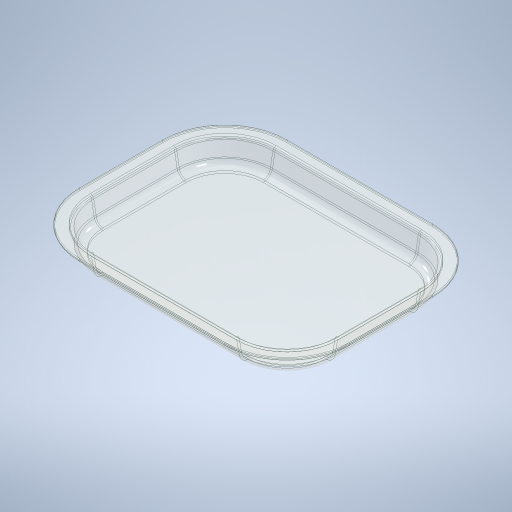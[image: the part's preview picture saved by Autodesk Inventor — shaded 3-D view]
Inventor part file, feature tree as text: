
AUTODESK INVENTOR PART (.ipt)
format: ipt  version: 2024 (Build 280153000, 153)  size: 461,312 bytes
history: native  units: mm
features: other x7, fillet x5, plane x3, sketch x3, mirror x2, extrude x1, shell x1, sweep x1, pattern_circular x1, revolve x1, loft x1, projected_geometry x1
ambient origin geometry x8: Origin, YZ Plane, XZ Plane, XY Plane, X Axis, Y Axis, Z Axis, Center Point
bodies: Volumenkörper1 (feature_tree)
feature tree (27):
  extrude  "Extrusion1"  Depth=70.0mm
  fillet  "Rundung1"  Radius=33.5mm
  other  "Flächenverjüngung1"
  fillet  "Rundung2"  Radius=70.0mm
  shell  "Wandung1"  Thickness=-1.745329mm
  sweep  "Sweeping1"
  fillet  "Rundung3"  Radius=20.0mm
  fillet  "Rundung4"  Radius=3.5mm
  fillet  "Rundung5"  [1 undecoded]
  plane  "Arbeitsebene1"
  plane  "Arbeitsebene2"
  plane  "Arbeitsebene3"
  other  "Trennen1"
  other  "Trennen2"
  other  "Trennen3"
  pattern_circular  "Runde Anordnung1"  [2 undecoded]
  revolve  "Umdrehung1"
  mirror  "Spiegeln1"
  mirror  "Spiegeln2"
  loft  "Erhebung1"
  sketch  "Skizze1"  dims[d0=350.0mm d1=260.0mm d2=33.5mm d3=0.0mm d4=70.0mm d5=-1.745329mm]
  sketch  "Skizze2"  dims[d6=10.0mm d7=3.5mm d8=20.0mm d9=3.5mm d10=0.0mm d11=0.0mm]
  other  "3D-Skizze1"
  sketch  "Skizze3"  dims[d12=5.0mm d13=1.5mm d14=1.0mm d15=20.0mm d16=360.0deg d18=90.0deg d19=0.0mm d20=90.0deg d21=0.0mm d22=90.0deg]
  projected_geometry  "Projizierte Kontur1"
  other  "Kanten1"
  other  "Kanten2"
note: 3 required parameter values undecoded (feature->parameter linkage not recoverable at this tier; creation-order binding heuristic only, values carry confidence <= 0.55)
